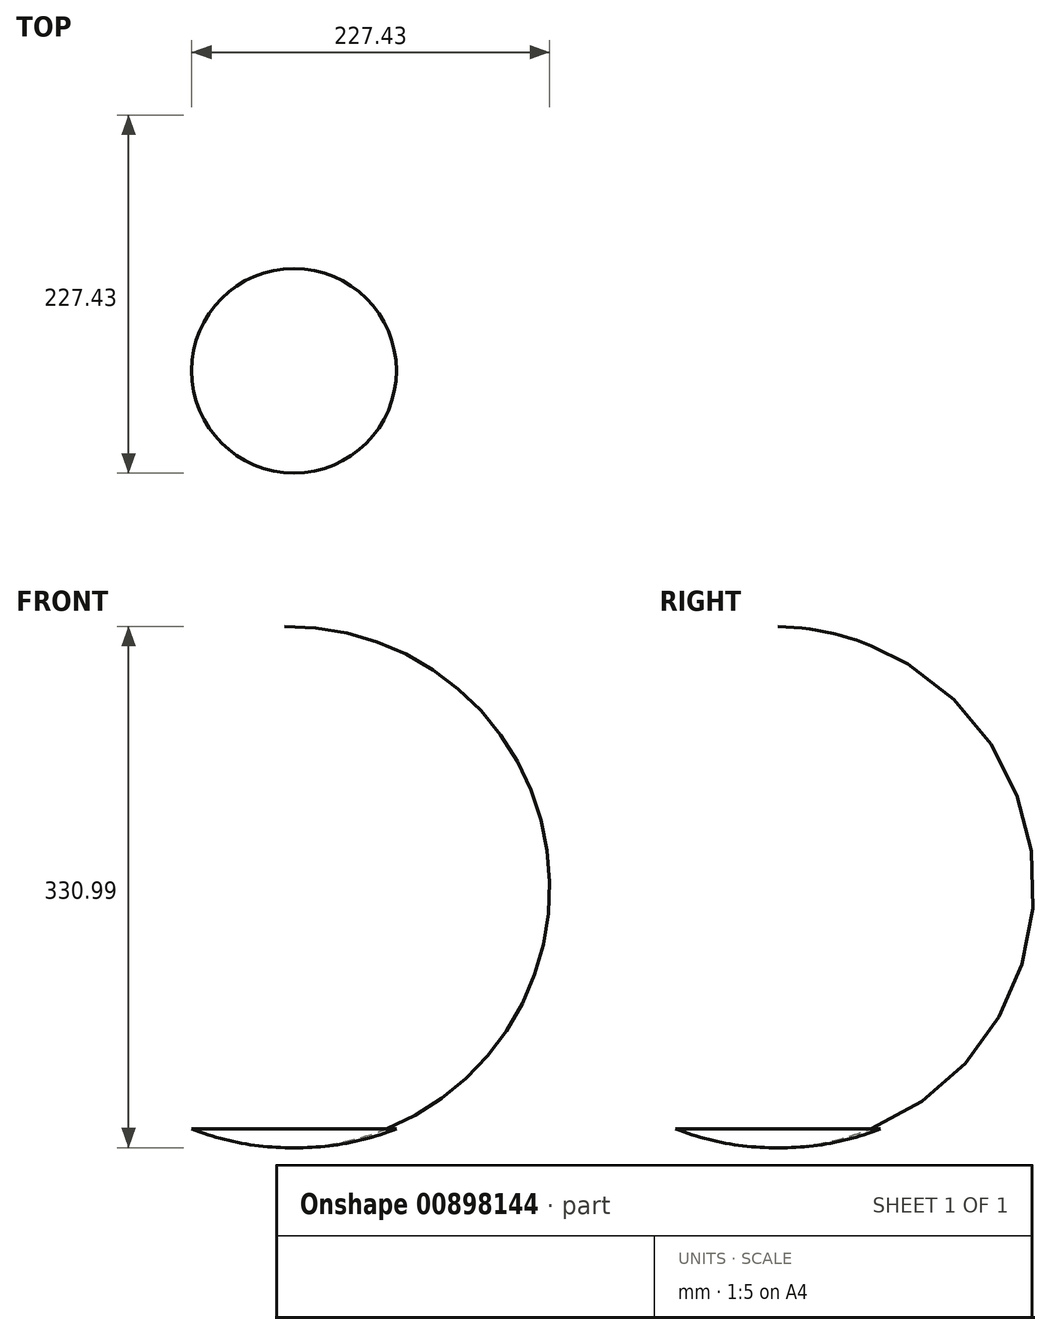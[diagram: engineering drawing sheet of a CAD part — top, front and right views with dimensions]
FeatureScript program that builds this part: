
annotation { "Feature Type Name" : "Feature", "Feature Type Description" : "" }
export const myFeature = defineFeature(function(context is Context, id is Id, definition is map)
    precondition{}
    {
        {
            var Q0;
            Q0=qCreatedBy(makeId("Front.planeOp"),FACE);
            var sketch = newSketch(context, id + "F0", { "sketchPlane" : qUnion([Q0])});
            skLineSegment(sketch, "E0", {"start": v(0, 0) * mm, "end": v(0, 68.4) * mm});
            skLineSegment(sketch, "E1", {"start": v(0, 0) * mm, "end": v(65, 0) * mm});
            skLineSegment(sketch, "E2", {"start": v(0, 0) * mm, "end": v(0, -12) * mm});
            skArc(sketch, "E3", {"start": v(0, -12) * mm, "mid": v(33.1, -9.28) * mm, "end": v(65, 0) * mm});
            skSolve(sketch);
        }
        {
            var Q0;
            Q0=makeQuery(id+"F0.imprint","IMPRINT",FACE,{"disambiguationData":[TD([[makeQuery(id+"F0.imprint","IMPRINT",EDGE,{"derivedFrom":sQuery(id+"F0.wireOp",EDGE,"E1")}),-1.0]])]});
            var Q1;
            Q1=sQuery(id+"F0.wireOp",EDGE,"E0");
            revolve(context, id + "F1", {"surfaceOperationType" : NewSurfaceOperationType.NEW, "entities" : qUnion([Q0]), "axis" : qUnion([Q1]), "revolveType" : RevolveType.FULL});
        }
    });
